# Revit family: Hager-Univers-IP54-D205-Cl.II-enclosure_metering-DE-de
name_source: partatom
category: Equipement électrique
units: mm (PartAtom-declared; Revit-internal decimal feet)

## family parameters
Configuration du panneau = Deux colonnes, circuits au sein
Cote de connecteur circulaire = Utiliser le diamètre
Couper avec des vides une fois chargée = Non
Hôte = Face
Partagée = Non
Point de calcul de pièce = Non
Type d'élément = Tableau de raccordement

## types (5) — shared parameters
Commentaires du type = Univers
EF000003 - Montageart = EV000384 - Aufputz
EF000007 - Farbe = EV000202 - weiß
EF000040 - Höhe = 500 mm  [stored 1.64042 ft]
EF000049 - Tiefe = 205 mm  [stored 0.672572 ft]
EF000116 - RAL-Nummer = 9010
EF000118 - Mit Montageplatte = Non
EF000218 - Einbautiefe = 205 mm  [stored 0.672572 ft]
EF000339 - Art der Abdeckung = EV004216 - Tür
EF001088 - Anbaumöglichkeit = Oui
EF001596 - Werkstoff des Gehäuses = EV000179 - Stahl
EF001613 - Funktionserhalt = EV000494 - ohne
EF003532 - Geeignet für Außengebrauch = Non
EF005474 - Schutzart (IP) = EV006419 - IP54
EF006244 - Transparenter Deckel/Tür = Non
EF006306 - Mit Schloss = Non
EF007800 - Geeignet für Blitzschutz = Non
EF008873 - Nennstrom (In) = 0 A
EF009170 - Materialstärke Gehäuse = 1 mm  [stored 0.00328084 ft]
EF009171 - Materialstärke Tür/Deckel = 1 mm  [stored 0.00328084 ft]
EF009212 - Ausführung Deckel = EV000116 - geschlossen
EF015940 - Deckel mit Überdruckentlastung = Non
Fabricant = Hager
HG000002 - Mit tür = Oui
HG000003 - Bereich = Univers
HG000006 - Unterputz = Non
HG000009 - Doppelflügeligen Tür = Non
HG000010 - Asymmetrische Türen = Non
HG000023 - Gehäuse mit doppeltem Querschnitt = Non
HG000024 - Höhe des unteren Teils = 800 mm  [stored 2.62467 ft]
HG000026 - Stehend auf dem Boden = Non
zero-valued in all types: EF000437 - Anzahl der Leitungseinführungen, EF001131 - Innentiefe, EF002950 - Breite in Teilungseinheiten, EF009554 - Anzahl der Öffnungen für Flanschplatten, Elévation par défaut, HG000027 - Sockelhöhe

## per-type parameters (varying)
| type | EF000008 - Breite | EF000266 - Anzahl der Reihen | EF004427 - Anzahl der Module | EF004464 - Art der Tür | HG000004 - Herstellerreferenz |
| Aufputz IP54 B1050 H500 T205  - ZB014W | 1050 mm | 12 | 144 | EV002646 - Einzel | ZB014W |
| Aufputz IP54 B1300 H500 T205  - ZB015W | 1300 mm  [stored 4.26509 ft] | 15 | 180 | EV002646 - Einzel | ZB015W |
| Aufputz IP54 B300 H500 T205  - ZB011W | 300 mm | 3 | 36 | EV002646 - Einzel | ZB011W |
| Aufputz IP54 B550 H500 T205  - ZB012W | 550 mm | 8 | 96 | EV002646 - Einzel | ZB012W |
| Aufputz IP54 B800 H500 T205  - ZB013W | 800 mm  [stored 2.62467 ft] | 9 | 108 | EV003602 - Doppel | ZB013W |

note: [stored X ft] marks values corroborated as IEEE doubles in the binary element streams (Revit-internal decimal feet)

## geometry (parser evidence)
native form markers: Sweep x10
no freeform markers — native parametric forms only
